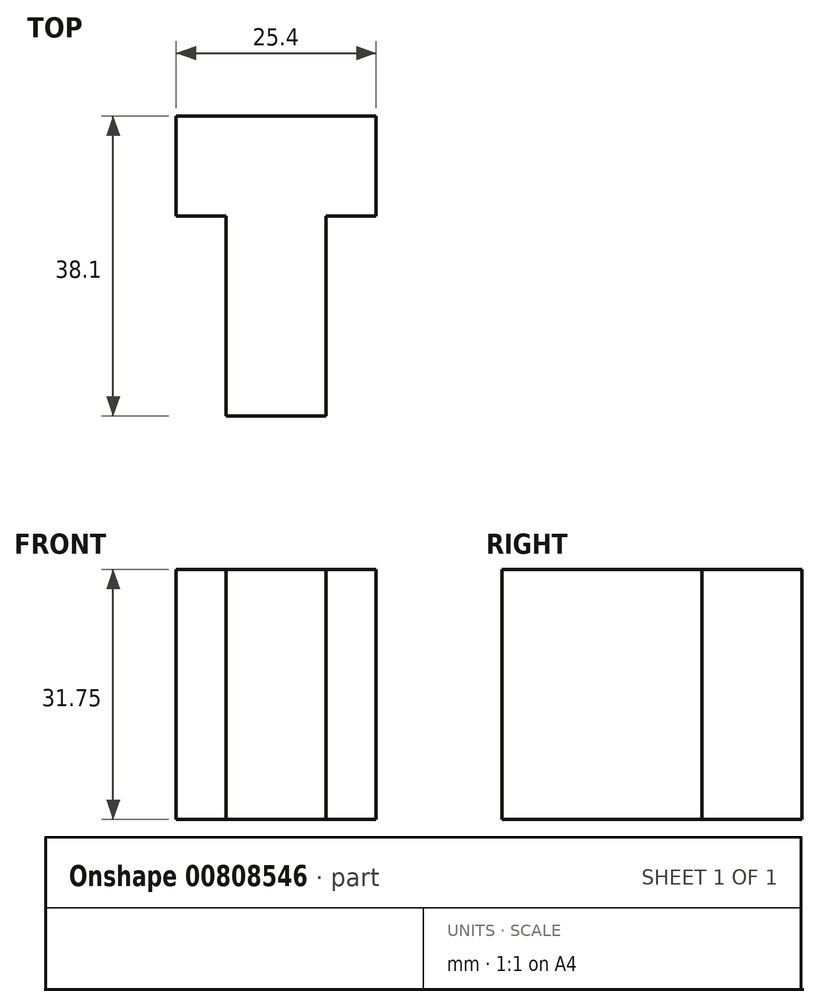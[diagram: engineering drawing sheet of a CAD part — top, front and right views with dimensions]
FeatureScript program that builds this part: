
annotation { "Feature Type Name" : "Feature", "Feature Type Description" : "" }
export const myFeature = defineFeature(function(context is Context, id is Id, definition is map)
    precondition{}
    {
        {
            var Q0;
            Q0=qCreatedBy(makeId("Top.planeOp"),FACE);
            var sketch = newSketch(context, id + "F0", { "sketchPlane" : qUnion([Q0])});
            skLineSegment(sketch, "E0", {"start": v(0, 0) * mm, "end": v(25.4, 0) * mm});
            skLineSegment(sketch, "E1", {"start": v(25.4, 0) * mm, "end": v(25.4, -12.7) * mm});
            skLineSegment(sketch, "E2", {"start": v(0, 0) * mm, "end": v(0, -12.7) * mm});
            skLineSegment(sketch, "E3", {"start": v(0, -12.7) * mm, "end": v(6.35, -12.7) * mm});
            skLineSegment(sketch, "E4", {"start": v(25.4, -12.7) * mm, "end": v(19.05, -12.7) * mm});
            skLineSegment(sketch, "E5", {"start": v(6.35, -12.7) * mm, "end": v(6.35, -38.1) * mm});
            skLineSegment(sketch, "E6", {"start": v(19.05, -12.7) * mm, "end": v(19.05, -38.1) * mm});
            skLineSegment(sketch, "E7", {"start": v(19.05, -38.1) * mm, "end": v(6.35, -38.1) * mm});
            skSolve(sketch);
        }
        {
            var Q0;
            Q0 = qSketchRegion(id + "F0", true);
            extrude(context, id + "F1", {"entities" : qUnion([Q0]), "depth" : 31.75 * mm, "offsetDistance" : 25.4 * mm});
        }
    });
